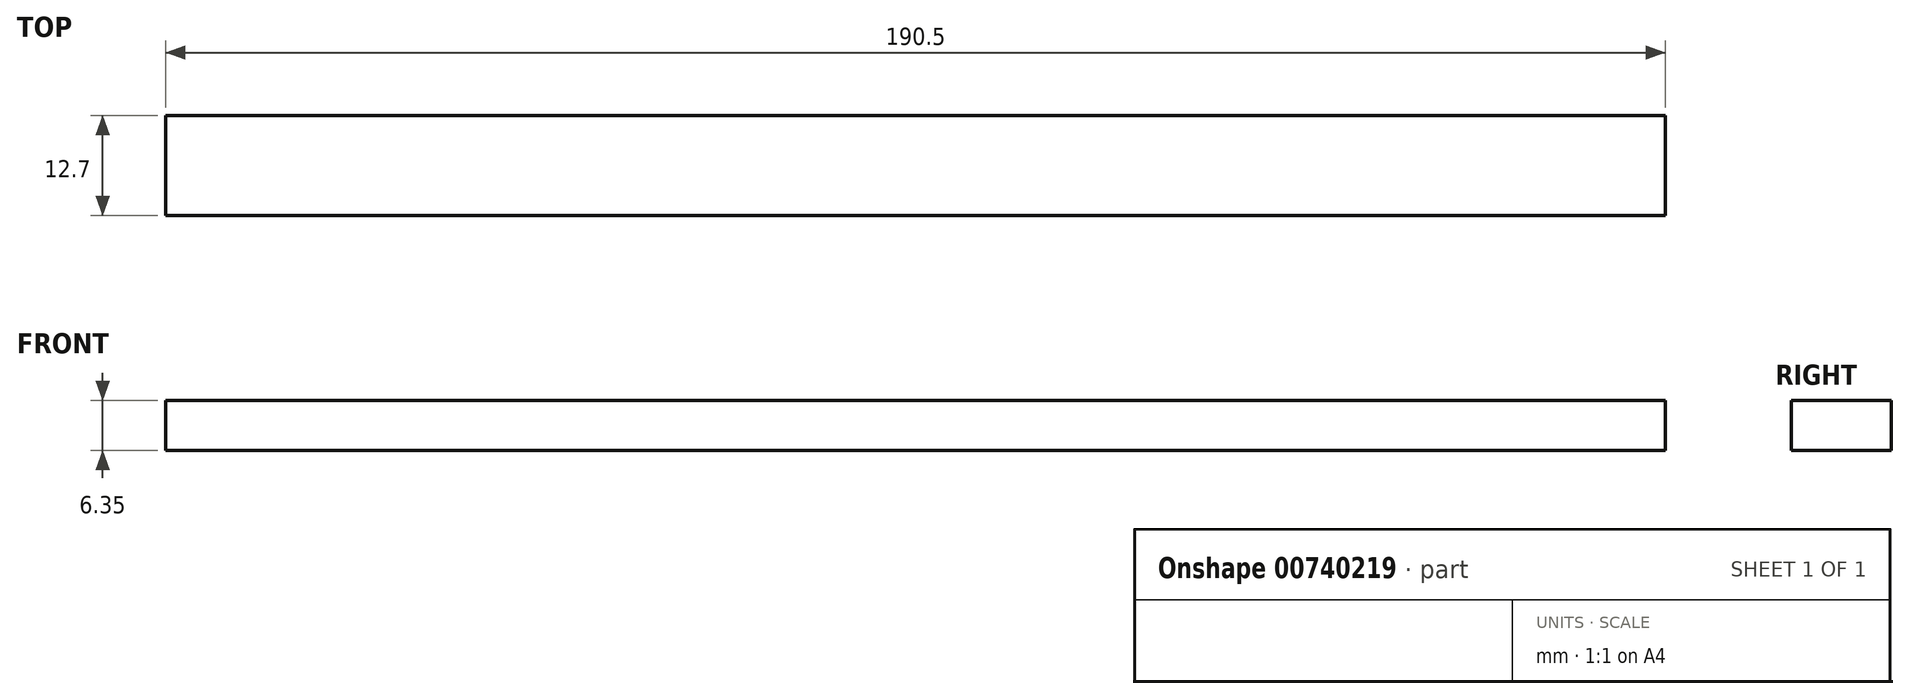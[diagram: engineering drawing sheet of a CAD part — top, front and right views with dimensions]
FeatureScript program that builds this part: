
annotation { "Feature Type Name" : "Feature", "Feature Type Description" : "" }
export const myFeature = defineFeature(function(context is Context, id is Id, definition is map)
    precondition{}
    {
        {
            var Q0;
            Q0=qCreatedBy(makeId("Top.planeOp"),FACE);
            var sketch = newSketch(context, id + "F0", { "sketchPlane" : qUnion([Q0])});
            skLineSegment(sketch, "E0.bottom", {"start": v(0, 0) * mm, "end": v(190.5, 0) * mm});
            skLineSegment(sketch, "E0.top", {"start": v(0, -12.7) * mm, "end": v(190.5, -12.7) * mm});
            skLineSegment(sketch, "E0.left", {"start": v(0, 0) * mm, "end": v(0, -12.7) * mm});
            skLineSegment(sketch, "E0.right", {"start": v(190.5, 0) * mm, "end": v(190.5, -12.7) * mm});
            skSolve(sketch);
        }
        {
            var Q0;
            Q0=makeQuery(id+"F0.imprint","IMPRINT",FACE,{"disambiguationData":[TD([[makeQuery(id+"F0.imprint","IMPRINT",EDGE,{"derivedFrom":sQuery(id+"F0.wireOp",EDGE,"E0.bottom")}),-1.0]])]});
            extrude(context, id + "F1", {"entities" : qUnion([Q0]), "depth" : 6.35 * mm, "offsetDistance" : 25.4 * mm});
        }
    });
